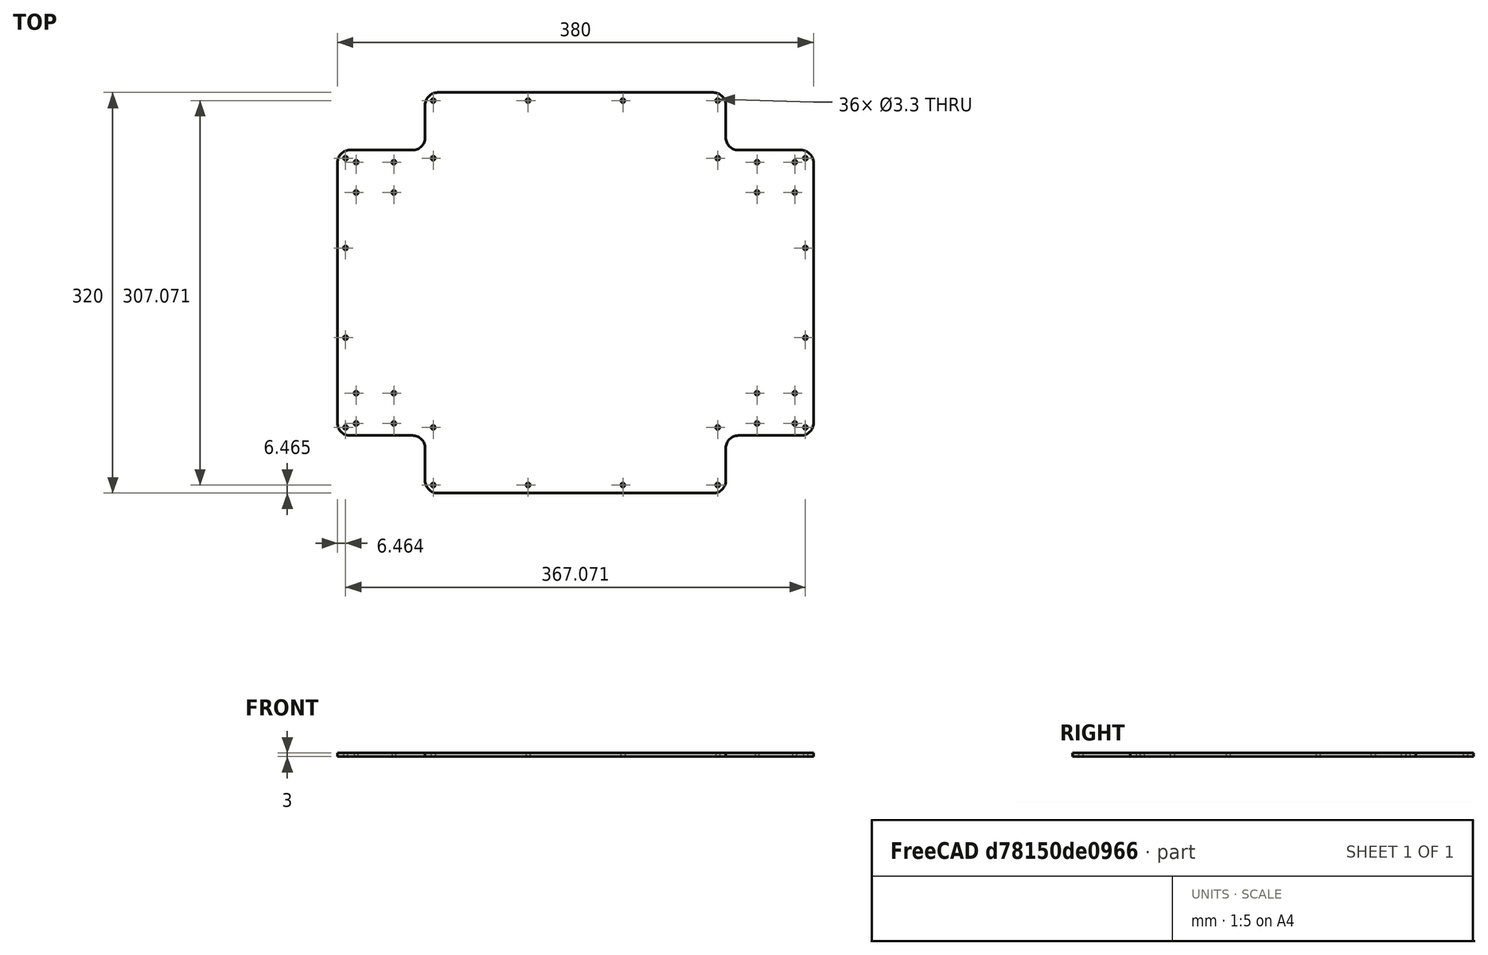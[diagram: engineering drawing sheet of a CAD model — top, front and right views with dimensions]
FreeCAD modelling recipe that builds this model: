
FCSTD DOCUMENT  (FreeCAD 1.0R39109 (Git))
Label: base_abajo
License: All rights reserved
LicenseURL: https://en.wikipedia.org/wiki/All_rights_reserved
objects: Part::Feature×1, PartDesign::FeatureBase×1, Sketcher::SketchObject×1, PartDesign::Body×1
note: 6 computed .brp shape members not serialized (recipe doc carries the construction recipe); baked Part::Feature solids carry a one-line shape summary decoded from their .brp

FEATURE [Part::Feature] Part__Feature  label="base_abajo v9"
  shape: bbox 380 x 320 x 3 mm, 62 faces (baked)
FEATURE [PartDesign::FeatureBase] BaseFeature
  BaseFeature = -> Part__Feature
  Suppressed = false
FEATURE [Sketcher::SketchObject] Sketch
  ArcFitTolerance = 1e-06
  AttachmentSupport = -> [BaseFeature]
  ExternalGeometry = -> [BaseFeature]
  FullyConstrained = true
  MakeInternals = false
  MapMode = 5
  Placement = pos=(0,0,3) rot=(0,0,1;0rad)
  sketch-geometry (11):
    g0: LineSegment [constr] StartX=-175.05 StartY=55.65 StartZ=0 EndX=-144.95 EndY=55.65 EndZ=0
    g1: LineSegment [constr] StartX=175.05 StartY=55.65 StartZ=0 EndX=144.95 EndY=55.65 EndZ=0
    g2: LineSegment StartX=160 StartY=55.65 StartZ=0 EndX=-160 EndY=55.65 EndZ=0
    g3: LineSegment StartX=-190 StartY=160 StartZ=0 EndX=190 EndY=160 EndZ=0
    g4: LineSegment [constr] StartX=-160 StartY=55.65 StartZ=0 EndX=-160 EndY=46 EndZ=0
    g5: LineSegment [constr] StartX=-175.05 StartY=264.35 StartZ=0 EndX=-144.95 EndY=264.35 EndZ=0
    g6: LineSegment [constr] StartX=-160 StartY=264.35 StartZ=0 EndX=-160 EndY=274 EndZ=0
    g7: LineSegment [constr] StartX=-160 StartY=46 StartZ=0 EndX=-160 EndY=16 EndZ=0
    g8: LineSegment [constr] StartX=-160 StartY=274 StartZ=0 EndX=-160 EndY=304 EndZ=0
    g9: LineSegment StartX=-160 StartY=304 StartZ=0 EndX=-160 EndY=16 EndZ=0
    g10: LineSegment StartX=0 StartY=320 StartZ=0 EndX=0 EndY=0 EndZ=0
  constraints (30):
    c: Coincident(g0,g-3)
    c: Coincident(g0,g-4)
    c: Coincident(g1,g-6)
    c: Coincident(g1,g-5)
    c: Symmetric(g1,g1,g2)
    c: Symmetric(g0,g0,g2)
    c: DistanceX(g2,g2) = 320
    c: Symmetric(g-7,g-7,g3)
    c: Symmetric(g-8,g-8,g3)
    c: DistanceX(g3,g3) = 380
    c: Coincident(g4,g2)
    c: PointOnObject(g4,g-10)
    c: Vertical(g4)
    c: Coincident(g5,g-11)
    c: Coincident(g5,g-12)
    c: Symmetric(g5,g5,g6)
    c: PointOnObject(g6,g-9)
    c: Vertical(g6)
    c: Distance(g7) = 30
    c: Coincident(g7,g4)
    c: Vertical(g7)
    c: Coincident(g8,g6)
    c: Vertical(g8)
    c: Equal(g8,g7)
    c: Coincident(g9,g8)
    c: Coincident(g9,g7)
    c: DistanceY(g9,g9) = 288
    c: Symmetric(g-13,g-13,g10)
    c: Symmetric(g-14,g-14,g10)
    c: DistanceY(g10,g10) = 320
FEATURE [PartDesign::Body] Body
  AllowCompound = false
  BaseFeature = -> Part__Feature
  Group = -> [BaseFeature,Sketch]
  Origin = -> Origin
  Tip = -> BaseFeature
